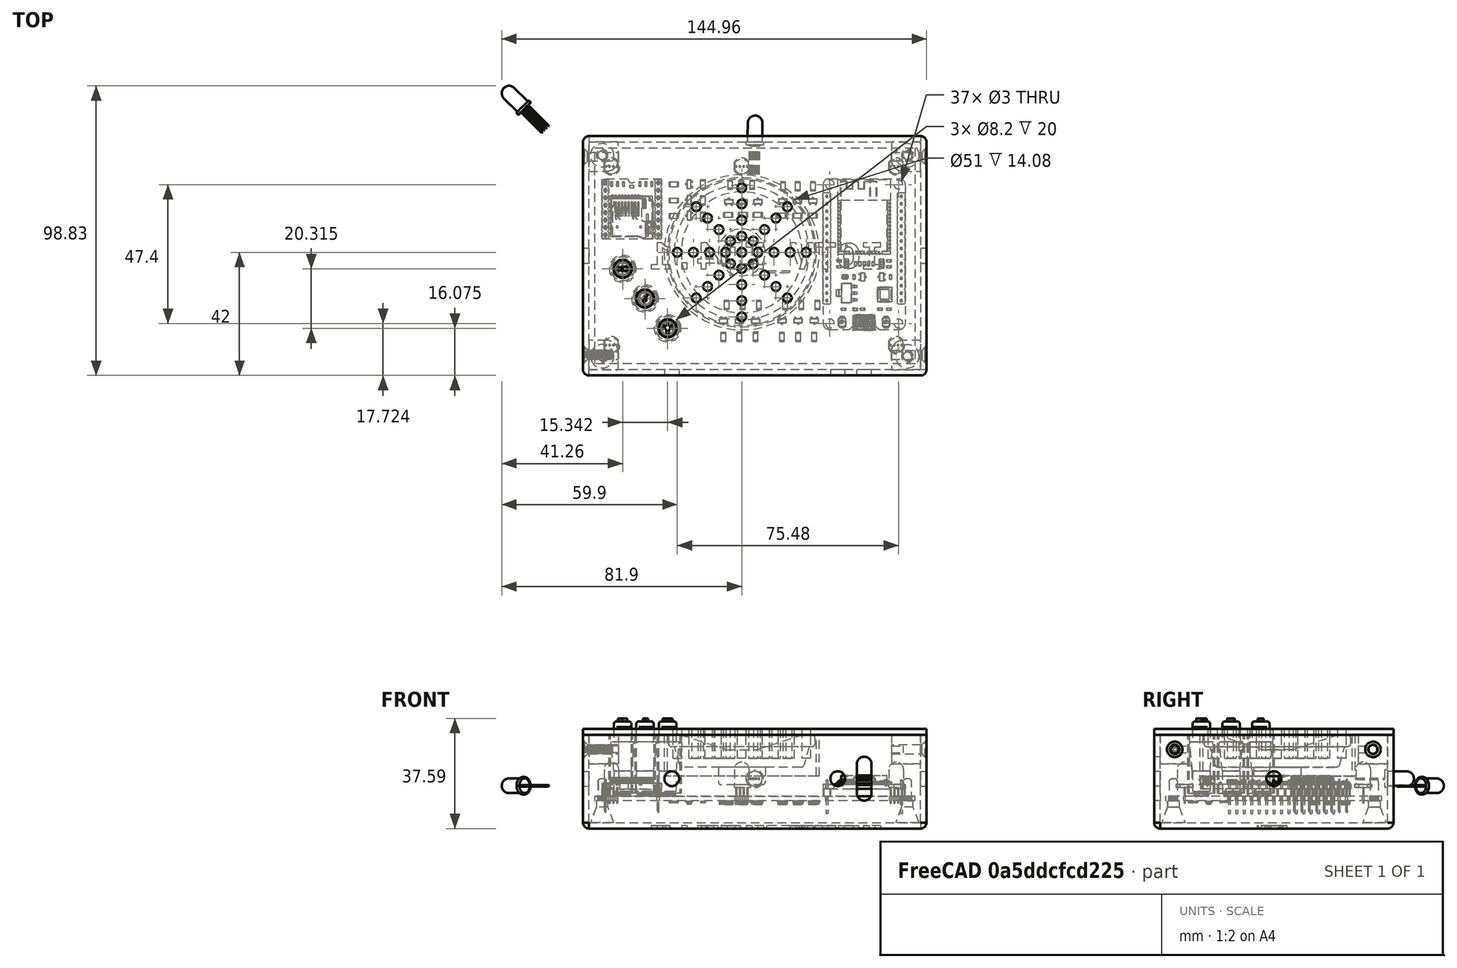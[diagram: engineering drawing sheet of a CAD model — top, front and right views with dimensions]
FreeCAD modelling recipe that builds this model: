
FCSTD DOCUMENT  (FreeCAD 0.20R)
Label: id4.1
License: All rights reserved
LicenseURL: http://en.wikipedia.org/wiki/All_rights_reserved
objects: PartDesign::Body×19, Part::Fillet×18, PartDesign::FeatureBase×17, Sketcher::SketchObject×15, Part::MultiFuse×13, Part::Cylinder×10, Part::FeaturePython×8, Part::Chamfer×8, Part::Extrusion×6, Part::Cut×6, PartDesign::Pocket×5, Part::Cone×4, PartDesign::ShapeBinder×4, Part::Box×4, App::Part×4, PartDesign::Fillet×2, PartDesign::Pad×2, Part::Compound×2, Part::Thickness×1, Part::Feature×1, +7 more types
note: 162 computed .brp shape members not serialized (recipe doc carries the construction recipe); baked Part::Feature solids carry a one-line shape summary decoded from their .brp

FEATURE [Sketcher::SketchObject] Sketch
  FullyConstrained = false
  MapMode = 5
  Placement = pos=(-170,95,8.58) rot=(0,0,1;0rad)
  sketch-geometry (4):
    g0: LineSegment StartX=114.84 StartY=-51.34 StartZ=0 EndX=228.06 EndY=-51.34 EndZ=0
    g1: LineSegment StartX=228.06 StartY=-51.34 StartZ=0 EndX=228.06 EndY=-129 EndZ=0
    g2: LineSegment StartX=228.06 StartY=-129 StartZ=0 EndX=114.84 EndY=-129 EndZ=0
    g3: LineSegment StartX=114.84 StartY=-129 StartZ=0 EndX=114.84 EndY=-51.34 EndZ=0
  constraints (8):
    c: Coincident(g0,g1)
    c: Coincident(g1,g2)
    c: Coincident(g2,g3)
    c: Coincident(g3,g0)
    c: Horizontal(g0)
    c: Horizontal(g2)
    c: Vertical(g1)
    c: Vertical(g3)
FEATURE [Part::Extrusion] Extrude
  Base = -> Sketch
  Dir = (0,0,1)
  DirMode = 2
  FaceMakerClass = Part::FaceMakerBullseye
  LengthFwd = 30
  LengthRev = 0
  Solid = true
  Symmetric = false
FEATURE [Part::Thickness] Thickness
  Faces = -> Extrude [Face6]
  Intersection = false
  Join = 0
  Mode = 0
  SelfIntersection = false
  Value = 2
FEATURE [Part::Feature] Feature001  label="Плата001"
  Placement = pos=(-170,95,16) rot=(0,0,1;0rad)
  shape: bbox 109.2 x 73.67 x 17.65 mm, 7789 faces, 158 solids (baked)
FEATURE [Part::FeaturePython] Screw001  label="M3x10-Винт001"  # Fasteners workbench fastener (typed FeaturePython)
  Placement = pos=(-57.16,-28.85,33.6) rot=(0,-1,0;1.5708rad)
  diameter = 4
  invert = false
  leftHanded = false
  length = 3
  lengthCustom = 10
  matchOuter = false
  offset = 0
  thread = true
  type = 47
FEATURE [Sketcher::SketchObject] Sketch004
  FullyConstrained = true
  MapMode = 5
  Placement = pos=(0,0,0) rot=(0.57735,0.57735,0.57735;2.0944rad)
  Support = -> [YZ_Plane]
FEATURE [Sketcher::SketchObject] Sketch001
  FullyConstrained = false
  MapMode = 5
  Placement = pos=(-170,95,17.58) rot=(0,0,1;0rad)
  Support = -> [Feature001]
  sketch-geometry (4):
    g0: Circle CenterX=119.361 CenterY=-55.8877 CenterZ=0 NormalX=0 NormalY=0 NormalZ=1 AngleXU=0 Radius=1.4
    g1: Circle CenterX=223.525 CenterY=-55.8927 CenterZ=0 NormalX=0 NormalY=0 NormalZ=1 AngleXU=0 Radius=1.4
    g2: Circle CenterX=119.376 CenterY=-124.461 CenterZ=0 NormalX=0 NormalY=0 NormalZ=1 AngleXU=0 Radius=1.4
    g3: Circle CenterX=223.508 CenterY=-124.479 CenterZ=0 NormalX=0 NormalY=0 NormalZ=1 AngleXU=0 Radius=1.4
  constraints (4):
    c: Diameter(g3) = 2.8
    c: Diameter(g2) = 2.8
    c: Diameter(g0) = 2.8
    c: Diameter(g1) = 2.8
FEATURE [Part::Extrusion] Extrude001
  Base = -> Sketch001
  Dir = (0,0,1)
  DirMode = 2
  FaceMakerClass = Part::FaceMakerBullseye
  LengthFwd = 15
  LengthRev = 0
  Placement = pos=(0,0,-9) rot=(0,0,1;0rad)
  Solid = true
  Symmetric = false
FEATURE [Part::Fillet] Fillet
  Base = -> Extrude001
  Edges = 1 edges r=1: [Edge6]
FEATURE [Part::Fillet] Fillet001
  Base = -> Fillet
  Edges = 1 edges r=1: [Edge13]
FEATURE [Part::Cone] Cone  label="Конус"
  Angle = 360
  AttacherType = Attacher::AttachEngine3D
  Height = 8
  Placement = pos=(-50.62,-29.46,8.58) rot=(0,0,1;0rad)
  Radius1 = 4
  Radius2 = 1
FEATURE [Part::Cylinder] Cylinder  label="Цилиндр"
  Angle = 360
  AttacherType = Attacher::AttachEngine3D
  FirstAngle = 0
  Height = 2.5
  Placement = pos=(-50.624,-29.4614,13.58) rot=(0,0,1;0rad)
  Radius = 2
  SecondAngle = 0
FEATURE [Part::Fillet] Fillet002
  Base = -> Fillet001
  Edges = 1 edges r=1: [Edge15]
FEATURE [Part::MultiFuse] Fusion
  Placement = pos=(-0.019282,68.5723,-1.8e-15) rot=(0,0,1;0rad)
  Shapes = -> [Cone,Cylinder]
FEATURE [Part::FeaturePython] Clone  label="Fusion001"  # Draft clone (typed FeaturePython)
  AttacherType = Attacher::AttachEngine3D
  Fuse = false
  Objects = -> [Fusion]
  Placement = pos=(104.145,68.5673,-1.8e-15) rot=(0,0,1;0rad)
  Scale = (1,1,1)
FEATURE [Part::FeaturePython] Clone001  label="Fusion002"  # Draft clone (typed FeaturePython)
  AttacherType = Attacher::AttachEngine3D
  Fuse = false
  Objects = -> [Clone]
  Placement = pos=(104.128,-0.018798,-1.8e-15) rot=(0,0,1;0rad)
  Scale = (1,1,1)
FEATURE [Part::FeaturePython] Clone002  label="Fusion003"  # Draft clone (typed FeaturePython)
  AttacherType = Attacher::AttachEngine3D
  Fuse = false
  Objects = -> [Clone001]
  Scale = (1,1,1)
FEATURE [Part::Fillet] Fillet003
  Base = -> Fillet002
  Edges = 1 edges r=1: [Edge17]
FEATURE [Part::Fillet] Fillet004
  Base = -> Fusion
  Edges = 1 edges r=0.5: [Edge4]
FEATURE [Part::Fillet] Fillet005
  Base = -> Clone002
  Edges = 1 edges r=0.5: [Edge4]
FEATURE [Part::Fillet] Fillet006
  Base = -> Clone001
  Edges = 1 edges r=0.5: [Edge4]
FEATURE [Part::Fillet] Fillet007
  Base = -> Clone
  Edges = 1 edges r=0.5: [Edge4]
FEATURE [Part::MultiFuse] Fusion001  label="Fusion004"
  Shapes = -> [Fillet007,Fillet003,Fillet004,Fillet005,Fillet006]
FEATURE [Part::MultiFuse] Fusion002  label="зависимость"
  Placement = pos=(6.25,0.25,-0.733338) rot=(0,0,1;0rad)
  Shapes = -> [Fusion001,Thickness]
FEATURE [PartDesign::FeatureBase] BaseFeature
  BaseFeature = -> Fusion002
FEATURE [PartDesign::Body] Body  label="корпус"
  BaseFeature = -> Fusion002
  Group = -> [BaseFeature,Sketch004]
  Origin = -> Origin
  Tip = -> BaseFeature
FEATURE [Sketcher::SketchObject] Sketch002
  ExternalGeometry = -> [BaseFeature]
  FullyConstrained = false
  MapMode = 5
  Support = -> [XY_Plane]
  sketch-geometry (8):
    g0: LineSegment StartX=58.06 StartY=45.66 StartZ=0 EndX=-55.16 EndY=45.66 EndZ=0
    g1: LineSegment StartX=-57.16 StartY=43.66 StartZ=0 EndX=-57.16 EndY=-34 EndZ=0
    g2: LineSegment StartX=-55.16 StartY=-36 StartZ=0 EndX=58.06 EndY=-36 EndZ=0
    g3: ArcOfCircle CenterX=-55.16 CenterY=43.66 CenterZ=0 NormalX=0 NormalY=0 NormalZ=1 AngleXU=0 Radius=2 StartAngle=1.5708 EndAngle=3.14159
    g4: ArcOfCircle CenterX=-55.16 CenterY=-34 CenterZ=0 NormalX=0 NormalY=0 NormalZ=1 AngleXU=0 Radius=2 StartAngle=3.14159 EndAngle=4.71239
    g5: LineSegment StartX=60.06 StartY=-34 StartZ=0 EndX=60.06 EndY=43.66 EndZ=0
    g6: ArcOfCircle CenterX=58.06 CenterY=43.66 CenterZ=0 NormalX=0 NormalY=0 NormalZ=1 AngleXU=0 Radius=2 StartAngle=-2.22e-14 EndAngle=1.5708
    g7: ArcOfCircle CenterX=58.06 CenterY=-34 CenterZ=0 NormalX=0 NormalY=0 NormalZ=1 AngleXU=0 Radius=2 StartAngle=4.71239 EndAngle=6.28319
  constraints (18):
    c: Coincident(g0,g-10)
    c: Coincident(g0,g-4)
    c: Coincident(g1,g-5)
    c: Coincident(g1,g-6)
    c: Coincident(g2,g-7)
    c: Coincident(g2,g-8)
    c: Coincident(g3,g1)
    c: Coincident(g3,g0)
    c: Coincident(g4,g2)
    c: Coincident(g4,g1)
    c: Tangent(g4,g-6)
    c: Coincident(g5,g-9)
    c: Coincident(g5,g-10)
    c: Coincident(g6,g5)
    c: Coincident(g6,g0)
    c: Tangent(g6,g-10)
    c: Coincident(g7,g2)
    c: Coincident(g7,g5)
FEATURE [Part::Extrusion] Extrude002  label="крышка"
  Base = -> Sketch002
  Dir = (0,0,1)
  DirMode = 2
  FaceMakerClass = Part::FaceMakerBullseye
  LengthFwd = 2
  LengthRev = 0
  Placement = pos=(0,0,39) rot=(0,0,1;0rad)
  Solid = true
  Symmetric = false
FEATURE [PartDesign::FeatureBase] BaseFeature001
  BaseFeature = -> Extrude002
  Placement = pos=(0,7.1e-15,-1.42) rot=(0,0,1;0rad)
FEATURE [PartDesign::Body] Body001  label="Крышка"
  BaseFeature = -> Extrude002
  Group = -> [BaseFeature001]
  Origin = -> Origin001
  Placement = pos=(0,0,40) rot=(0,0,1;0rad)
  Tip = -> BaseFeature001
FEATURE [Sketcher::SketchObject] Sketch003
  ExternalGeometry = -> [BaseFeature]
  FullyConstrained = true
  MapMode = 5
  Placement = pos=(0,0,38.58) rot=(0,0,1;0rad)
  Support = -> [BaseFeature]
  sketch-geometry (4):
    g0: LineSegment StartX=-55.16 StartY=-34 StartZ=0 EndX=-45.16 EndY=-34 EndZ=0
    g1: LineSegment StartX=-45.16 StartY=-34 StartZ=0 EndX=-45.16 EndY=-24 EndZ=0
    g2: LineSegment StartX=-45.16 StartY=-24 StartZ=0 EndX=-55.16 EndY=-24 EndZ=0
    g3: LineSegment StartX=-55.16 StartY=-24 StartZ=0 EndX=-55.16 EndY=-34 EndZ=0
  constraints (11):
    c: Coincident(g0,g1)
    c: Coincident(g1,g2)
    c: Coincident(g2,g3)
    c: Coincident(g3,g0)
    c: Horizontal(g0)
    c: Horizontal(g2)
    c: Vertical(g1)
    c: Vertical(g3)
    c: Coincident(g0,g-4)
    c: Distance(g2) = 10
    c: Distance(g3) = 10
FEATURE [Part::Extrusion] Extrude003
  Base = -> Sketch003
  Dir = (0,0,1)
  DirMode = 2
  FaceMakerClass = Part::FaceMakerBullseye
  LengthFwd = 10
  LengthRev = 0
  Reversed = true
  Solid = true
  Symmetric = false
FEATURE [PartDesign::ShapeBinder] ShapeBinder
  Placement = pos=(-57.16,-28.85,33.6) rot=(0,-1,0;1.5708rad)
  Support = -> [Screw001]
  TraceSupport = false
FEATURE [PartDesign::ShapeBinder] ShapeBinder001
  Placement = pos=(-57.16,-28.85,33.6) rot=(0,-1,0;1.5708rad)
  Support = -> [Screw001]
  TraceSupport = false
FEATURE [PartDesign::ShapeBinder] ShapeBinder002
  Placement = pos=(-57.16,-28.85,33.6) rot=(0,-1,0;1.5708rad)
  Support = -> [Screw001]
  TraceSupport = false
FEATURE [PartDesign::ShapeBinder] ShapeBinder003
  Placement = pos=(-57.16,-28.85,33.6) rot=(0,-1,0;1.5708rad)
  Support = -> [Screw001]
  TraceSupport = false
FEATURE [Part::Loft] Loft
  Closed = false
  MaxDegree = 5
  Placement = pos=(0,-0.15,-0.02) rot=(0,0,1;0rad)
  Ruled = true
  Sections = -> [ShapeBinder,ShapeBinder003,ShapeBinder001,ShapeBinder002]
  Solid = true
FEATURE [PartDesign::FeatureBase] Clone003
  BaseFeature = -> Loft
  Placement = pos=(26.1,-88.15,-67.18) rot=(0,0,1;0rad)
FEATURE [PartDesign::Body] Body003
  BaseFeature = -> Loft
  Group = -> [Clone003]
  Origin = -> Origin003
  Placement = pos=(29,88,0) rot=(0,1,0;3.14159rad)
  Tip = -> Clone003
FEATURE [PartDesign::FeatureBase] Clone004
  BaseFeature = -> Loft
  Placement = pos=(8,15.51,-0.02) rot=(0,0,1;0rad)
FEATURE [PartDesign::Body] Body004
  BaseFeature = -> Loft
  Group = -> [Clone004]
  Origin = -> Origin004
  Placement = pos=(-8,52,0) rot=(0,0,1;0rad)
  Tip = -> Clone004
FEATURE [PartDesign::FeatureBase] Clone005
  BaseFeature = -> Loft
  Placement = pos=(67.1,-33.49,-67.18) rot=(0,0,1;0rad)
FEATURE [PartDesign::Body] Body005
  BaseFeature = -> Loft
  Group = -> [Clone005]
  Origin = -> Origin005
  Placement = pos=(70,101,0) rot=(0,1,0;3.14159rad)
  Tip = -> Clone005
FEATURE [PartDesign::FeatureBase] Clone006
  BaseFeature = -> Extrude003
  Placement = pos=(58.22,-6,0) rot=(0,0,1;0rad)
FEATURE [PartDesign::Body] Body006
  BaseFeature = -> Extrude003
  Group = -> [Clone006]
  Origin = -> Origin006
  Placement = pos=(45,6,0) rot=(0,0,1;0rad)
  Tip = -> Clone006
FEATURE [PartDesign::FeatureBase] Clone007
  BaseFeature = -> Extrude003
  Placement = pos=(-10,27.66,0) rot=(0,0,1;0rad)
FEATURE [PartDesign::Body] Body007
  BaseFeature = -> Extrude003
  Group = -> [Clone007]
  Origin = -> Origin007
  Placement = pos=(10,40,0) rot=(0,0,1;0rad)
  Tip = -> Clone007
FEATURE [PartDesign::FeatureBase] Clone008
  BaseFeature = -> Extrude003
  Placement = pos=(89.22,45.66,0) rot=(0,0,1;0rad)
FEATURE [PartDesign::Body] Body008
  BaseFeature = -> Extrude003
  Group = -> [Clone008]
  Origin = -> Origin008
  Placement = pos=(14,22,0) rot=(0,0,1;0rad)
  Tip = -> Clone008
FEATURE [Part::Cylinder] Cylinder001  label="Цилиндр001"
  Angle = 360
  AttacherType = Attacher::AttachEngine3D
  FirstAngle = 0
  Height = 141
  Placement = pos=(69.84,-29,33.58) rot=(0,-1,0;1.5708rad)
  Radius = 1.5
  SecondAngle = 0
FEATURE [Part::FeaturePython] Clone009  label="Цилиндр002"  # Draft clone (typed FeaturePython)
  AttacherType = Attacher::AttachEngine3D
  Fuse = false
  Objects = -> [Cylinder001]
  Placement = pos=(73.06,38.66,33.58) rot=(0,-1,0;1.5708rad)
  Scale = (1,1,1)
FEATURE [Part::MultiFuse] Fusion003  label="Fusion006"
  Shapes = -> [Body008,Body007,Body006,Extrude003]
FEATURE [Part::MultiFuse] Fusion004  label="Fusion007"
  Shapes = -> [Loft,Body003,Body004,Body005]
FEATURE [Part::Cut] Cut
  Base = -> Body
  Tool = -> Fusion004
FEATURE [PartDesign::FeatureBase] Clone010
  BaseFeature = -> Clone009
  Placement = pos=(73.06,38.66,33.58) rot=(0,-1,0;1.5708rad)
FEATURE [PartDesign::Body] Body009
  BaseFeature = -> Clone009
  Group = -> [Clone010]
  Origin = -> Origin009
  Tip = -> Clone010
FEATURE [PartDesign::FeatureBase] Clone011
  BaseFeature = -> Cylinder001
  Placement = pos=(69.84,-29,33.58) rot=(0,-1,0;1.5708rad)
FEATURE [PartDesign::Body] Body010
  BaseFeature = -> Cylinder001
  Group = -> [Clone011]
  Origin = -> Origin010
  Tip = -> Clone011
FEATURE [Part::Cut] Cut001
  Base = -> Cut
  Tool = -> Clone009
FEATURE [Part::Cut] Cut002  label="зависимость корпус001"
  Base = -> Cut001
  Tool = -> Cylinder001
FEATURE [Part::MultiFuse] Fusion005  label="Fusion008"
  Shapes = -> [Body009,Body010]
FEATURE [Part::Cut] Cut003
  Base = -> Fusion003
  Tool = -> Fusion005
FEATURE [Part::MultiFuse] Fusion006  label="зависимость001"
  Shapes = -> [Cut003,Body001]
FEATURE [PartDesign::FeatureBase] Clone012
  BaseFeature = -> Fusion006
FEATURE [PartDesign::Body] Body011  label="крышка002"
  BaseFeature = -> Fusion006
  Group = -> [Clone012]
  Origin = -> Origin013
  Tip = -> Clone012
FEATURE [Part::Box] Box004  label="Куб004"
  AttacherType = Attacher::AttachEngine3D
  Height = 10
  Length = 0.5
  Placement = pos=(-2,-0.25,-10) rot=(0,0,1;0rad)
  Width = 0.5
FEATURE [Part::Box] Box005  label="Куб005"
  AttacherType = Attacher::AttachEngine3D
  Height = 10
  Length = 0.5
  Placement = pos=(-2,-0.25,-10) rot=(0,0,1;0rad)
  Width = 0.5
FEATURE [Part::Box] Box006  label="Куб006"
  AttacherType = Attacher::AttachEngine3D
  Height = 10
  Length = 0.5
  Placement = pos=(-2,-0.25,-10) rot=(0,0,1;0rad)
  Width = 0.5
FEATURE [Part::Box] Box007  label="Куб007"
  AttacherType = Attacher::AttachEngine3D
  Height = 10
  Length = 0.5
  Placement = pos=(-2,-0.25,-10) rot=(0,0,1;0rad)
  Width = 0.5
FEATURE [Part::Chamfer] Chamfer008
  Base = -> Box004
  Edges = 1 edges r=0.2: [Edge9]
FEATURE [Part::Chamfer] Chamfer009
  Base = -> Chamfer008
  Edges = 1 edges r=0.2: [Edge14]
FEATURE [Part::Chamfer] Chamfer010
  Base = -> Box005
  Edges = 1 edges r=0.2: [Edge9]
FEATURE [Part::Chamfer] Chamfer011
  Base = -> Chamfer010
  Edges = 1 edges r=0.2: [Edge14]
  Placement = pos=(1,0,0) rot=(0,0,1;0rad)
FEATURE [Part::Chamfer] Chamfer012
  Base = -> Box006
  Edges = 1 edges r=0.2: [Edge9]
FEATURE [Part::Chamfer] Chamfer013
  Base = -> Chamfer012
  Edges = 1 edges r=0.2: [Edge14]
  Placement = pos=(2,0,0) rot=(0,0,1;0rad)
FEATURE [Part::Chamfer] Chamfer014
  Base = -> Box007
  Edges = 1 edges r=0.2: [Edge9]
FEATURE [Part::Chamfer] Chamfer015
  Base = -> Chamfer014
  Edges = 1 edges r=0.2: [Edge14]
  Placement = pos=(3,0,0) rot=(0,0,1;0rad)
FEATURE [Part::Cylinder] Cylinder021  label="Цилиндр021"
  Angle = 360
  AttacherType = Attacher::AttachEngine3D
  FirstAngle = 0
  Height = 10
  Radius = 2.5
  SecondAngle = 0
FEATURE [Part::Cylinder] Cylinder022  label="Цилиндр022"
  Angle = 360
  AttacherType = Attacher::AttachEngine3D
  FirstAngle = 0
  Height = 1
  Radius = 3
  SecondAngle = 0
FEATURE [Part::Fillet] Fillet014
  Base = -> Cylinder022
  Edges = 2 edges r=0.2: [Edge2,Edge3]
FEATURE [Part::MultiFuse] Fusion014
  Placement = pos=(0.25,0,0) rot=(0,0,1;0rad)
  Shapes = -> [Chamfer015,Chamfer009,Chamfer011,Chamfer013]
FEATURE [Sketcher::SketchObject] Sketch013
  FullyConstrained = true
  Placement = pos=(0,0,0) rot=(1,0,0;1.5708rad)
  sketch-geometry (10):
    g0: LineSegment StartX=0 StartY=0 StartZ=0 EndX=-25 EndY=0 EndZ=0
    g1: LineSegment StartX=-25 StartY=0 StartZ=0 EndX=-25 EndY=4 EndZ=0
    g2: LineSegment StartX=-25 StartY=4 StartZ=0 EndX=-23 EndY=4 EndZ=0
    g3: LineSegment StartX=-23 StartY=4 StartZ=0 EndX=-21 EndY=11 EndZ=0
    g4: LineSegment StartX=-21 StartY=11 StartZ=0 EndX=0 EndY=11 EndZ=0
    g5: LineSegment StartX=-21 StartY=11 StartZ=0 EndX=-21 EndY=0 EndZ=0
    g6: LineSegment StartX=-21 StartY=11 StartZ=0 EndX=-8 EndY=11 EndZ=0
    g7: LineSegment StartX=-8 StartY=11 StartZ=0 EndX=-8 EndY=17 EndZ=0
    g8: LineSegment StartX=-8 StartY=17 StartZ=0 EndX=0 EndY=17 EndZ=0
    g9: LineSegment StartX=0 StartY=17 StartZ=0 EndX=0 EndY=0 EndZ=0
  constraints (29):
    c: Coincident(g0,g-1)
    c: PointOnObject(g0,g-1)
    c: Coincident(g1,g0)
    c: Vertical(g1)
    c: Distance(g0) = 25
    c: Distance(g1) = 4
    c: Coincident(g2,g1)
    c: Horizontal(g2)
    c: Distance(g2) = 2
    c: Coincident(g3,g2)
    c: Coincident(g4,g3)
    c: PointOnObject(g4,g-2)
    c: Horizontal(g4)
    c: Distance(g4) = 21
    c: Coincident(g5,g3)
    c: PointOnObject(g5,g0)
    c: Vertical(g5)
    c: Distance(g5) = 11
    c: Coincident(g6,g3)
    c: PointOnObject(g6,g4)
    c: Distance(g6,g4) = 8
    c: Coincident(g7,g6)
    c: Vertical(g7)
    c: Distance(g7) = 6
    c: Coincident(g8,g7)
    c: Horizontal(g8)
    c: PointOnObject(g8,g-2)
    c: Coincident(g9,g8)
    c: Coincident(g9,g0)
FEATURE [Part::Revolution] Revolve
  Angle = 360
  Axis = (0,0,1)
  Base = (0,0,0)
  FaceMakerClass = Part::FaceMakerBullseye
  Solid = true
  Source = -> Sketch013
  Symmetric = false
FEATURE [Part::Fillet] Fillet017
  Base = -> Revolve
  Edges = 2 edges r=1: [Edge5,Edge8]
FEATURE [Part::Fillet] Fillet018
  Base = -> Fillet017
  Edges = 1 edges r=1: [Edge6]
FEATURE [PartDesign::FeatureBase] BaseFeature002
  BaseFeature = -> Fillet018
FEATURE [Sketcher::SketchObject] Sketch014
  FullyConstrained = false
  MapMode = 5
  Placement = pos=(0,0,0) rot=(1,0,0;3.14159rad)
  Support = -> [BaseFeature002]
  sketch-geometry (1):
    g0: Circle CenterX=0 CenterY=0 CenterZ=0 NormalX=0 NormalY=0 NormalZ=1 AngleXU=0 Radius=20.6628
  constraints (1):
    c: Coincident(g0,g-1)
FEATURE [PartDesign::Pocket] Pocket
  BaseFeature = -> BaseFeature002
  Direction = (0,0,1)
  Length = 5
  Length2 = 5
  Profile = -> Sketch014
  ReferenceAxis = -> Sketch014 [N_Axis]
  TaperAngle = -72
  Type = 0
FEATURE [PartDesign::Fillet] Fillet019
  Base = -> Pocket [Edge8]
  BaseFeature = -> Pocket
  Radius = 1
  SupportTransform = false
  UseAllEdges = false
FEATURE [PartDesign::Body] Body014  label="динамик"
  BaseFeature = -> Fillet018
  Group = -> [BaseFeature002,Sketch014,Pocket,Fillet019]
  Origin = -> Origin016
  Placement = pos=(-3,6,38.5) rot=(0,1,0;3.14159rad)
  Tip = -> Fillet019
FEATURE [Sketcher::SketchObject] Sketch015
  FullyConstrained = true
  MapMode = 5
  Support = -> [XY_Plane017]
  sketch-geometry (1):
    g0: Circle CenterX=0 CenterY=0 CenterZ=0 NormalX=0 NormalY=0 NormalZ=1 AngleXU=0 Radius=25.5
  constraints (2):
    c: Coincident(g0,g-1)
    c: Diameter(g0) = 51
FEATURE [PartDesign::Pad] Pad
  Direction = (0,0,1)
  Length = 15
  Length2 = 10
  Profile = -> Sketch015
  ReferenceAxis = -> Sketch015 [N_Axis]
  Type = 0
FEATURE [PartDesign::Thickness] Thickness001
  Base = -> Pad [Face2]
  BaseFeature = -> Pad
  Intersection = false
  Join = 0
  Mode = 0
  SupportTransform = false
  Value = 1
FEATURE [PartDesign::Body] Body015  label="капсулю динамика"
  Group = -> [Sketch015,Pad,Thickness001]
  Origin = -> Origin017
  Placement = pos=(-3,6,24.5) rot=(0,0,1;0rad)
  Tip = -> Thickness001
FEATURE [PartDesign::AdditiveCylinder] Cylinder023
  Angle = 360
  AttacherType = Attacher::AttachEngine3D
  FirstAngle = 0
  Height = 10
  Placement = pos=(-3,6,30.5) rot=(0,0,1;0rad)
  Radius = 1.5
  SecondAngle = 0
FEATURE [Part::FeaturePython] Array  # Draft array (typed FeaturePython)
  AlwaysSyncPlacement = false
  Angle = 360
  ArrayType = 0
  Axis = (0,0,1)
  Base = -> Cylinder023
  Center = (0,0,0)
  Count = 5
  ExpandArray = false
  Fuse = false
  IntervalAxis = (0,0,0)
  IntervalX = (5.5,0,0)
  IntervalY = (0,100,0)
  IntervalZ = (0,0,100)
  NumberCircles = 3
  NumberPolar = 5
  NumberX = 5
  NumberY = 1
  NumberZ = 1
  PlacementList = 5 placements: arithmetic series from (-3,6,30.5) step (5.5,0,0) to (19,6,30.5)
  RadialDistance = 50
  ScaleList = (5) [(1,1,1),(1,1,1),(1,1,1),(1,1,1),(1,1,1)]
  Symmetry = 1
  TangentialDistance = 25
FEATURE [Part::FeaturePython] Array001  # Draft array (typed FeaturePython)
  AlwaysSyncPlacement = false
  Angle = 360
  ArrayType = 1
  Axis = (0,0,1)
  Base = -> Array
  Center = (-3,6,39.5)
  Count = 8
  ExpandArray = false
  Fuse = false
  IntervalAxis = (0,0,0)
  IntervalX = (50,0,0)
  IntervalY = (0,50,0)
  IntervalZ = (0,0,50)
  NumberCircles = 2
  NumberPolar = 8
  NumberX = 2
  NumberY = 2
  NumberZ = 1
  Placement = pos=(0,0,7) rot=(0,0,1;0rad)
  PlacementList = 8 placements: [(0,0,0),(3.36396,3.87868,0),(3,9,0),(-0.87868,12.364,0),(-6,12,0),(-9.36396,8.12132,0),(-9,3,0),(-5.12132,-0.363961,0)]
  RadialDistance = 20
  ScaleList = (8) [(1,1,1),(1,1,1),(1,1,1),(1,1,1),(1,1,1),(1,1,1),(1,1,1),(1,1,1)]
  Symmetry = 1
  TangentialDistance = 15
FEATURE [Part::FeaturePython] Clone016  label="Array002"  # Draft clone (typed FeaturePython)
  AttacherType = Attacher::AttachEngine3D
  Fuse = false
  Objects = -> [Array001]
  Scale = (1,1,1)
FEATURE [Part::MultiFuse] Fusion015
  Shapes = -> [Body011,Body015]
FEATURE [Part::Cut] Cut004
  Base = -> Fusion015
  Tool = -> Array001
FEATURE [PartDesign::FeatureBase] Clone017
  BaseFeature = -> Cut004
FEATURE [PartDesign::FeatureBase] Clone018
  BaseFeature = -> Cut002
FEATURE [Part::Fillet] Fillet013
  Base = -> Cylinder021
  Edges = 1 edges r=2.5: [Edge3]
FEATURE [Part::Compound] Compound006
  Links = -> [Fusion014,Fillet014,Fillet013]
  Placement = pos=(-77.1,55.03,21.17) rot=(-0.281085,0.678598,0.678598;3.68962rad)
FEATURE [PartDesign::Boolean] Boolean001
  Group = -> [Chamfer008,Chamfer010,Fillet013,Chamfer011,Chamfer012,Compound006,Cylinder022,Chamfer013,Chamfer014,Chamfer015,Fusion014,Fillet014,Box004,Cylinder021,Box005,Box006,Box007,Chamfer009]
  Placement = pos=(12.1122,-20.0773,-7.88146) rot=(0,0,1;0rad)
  Type = 0
FEATURE [PartDesign::Body] Body013
  Group = -> [Boolean001]
  Origin = -> Origin015
  Placement = pos=(21.434,-28.3683,10.2915) rot=(0,0,-1;0.802851rad)
  Tip = -> Boolean001
FEATURE [App::Part] Part002  label="не печатать"
  Group = -> [Fillet018,Revolve,Fillet017,Sketch013,Body014,Body013,Fusion002,Cylinder,Sketch,Thickness,Fillet002,Extrude001,Clone001,Sketch001,Fusion001,Extrude,Clone,Clone002,Fillet,Fillet005,Fillet004,Fillet001,Fillet007,Fillet006,Cone,Fusion,Fillet003,Feature001]
  Origin = -> Origin019
FEATURE [Sketcher::SketchObject] Sketch016
  ExternalGeometry = -> [Clone018]
  FullyConstrained = true
  MapMode = 5
  Placement = pos=(0,-36,0) rot=(1,0,0;1.5708rad)
  Support = -> [Cut002]
  sketch-geometry (12):
    g0: LineSegment StartX=-55.16 StartY=38.58 StartZ=0 EndX=58.06 EndY=8.58 EndZ=0
    g1: LineSegment StartX=-55.16 StartY=8.58 StartZ=0 EndX=58.06 EndY=38.58 EndZ=0
    g2: GeomPoint X=1.45 Y=23.58 Z=0
    g3: LineSegment StartX=1.45 StartY=8.58 StartZ=0 EndX=1.45 EndY=38.58 EndZ=0
    g4: LineSegment StartX=-55.16 StartY=38.58 StartZ=0 EndX=1.45 EndY=8.58 EndZ=0
    g5: LineSegment StartX=-55.16 StartY=8.58 StartZ=0 EndX=1.45 EndY=38.58 EndZ=0
    g6: LineSegment StartX=1.45 StartY=8.58 StartZ=0 EndX=58.06 EndY=38.58 EndZ=0
    g7: LineSegment StartX=58.06 StartY=8.58 StartZ=0 EndX=1.45 EndY=38.58 EndZ=0
    g8: GeomPoint X=29.755 Y=23.58 Z=0
    g9: Circle CenterX=29.755 CenterY=23.58 CenterZ=0 NormalX=0 NormalY=0 NormalZ=1 AngleXU=0 Radius=2.525
    g10: GeomPoint X=-26.855 Y=23.58 Z=0
    g11: Circle CenterX=-26.855 CenterY=23.58 CenterZ=0 NormalX=0 NormalY=0 NormalZ=1 AngleXU=0 Radius=2.525
  constraints (26):
    c: Coincident(g0,g-5)
    c: Coincident(g0,g-6)
    c: Coincident(g1,g-6)
    c: Coincident(g1,g-5)
    c: PointOnObject(g2,g1)
    c: PointOnObject(g2,g0)
    c: PointOnObject(g3,g-6)
    c: PointOnObject(g3,g-5)
    c: Vertical(g3)
    c: PointOnObject(g2,g3)
    c: Coincident(g4,g0)
    c: Coincident(g4,g3)
    c: Coincident(g5,g1)
    c: Coincident(g5,g3)
    c: Coincident(g6,g3)
    c: Coincident(g6,g1)
    c: Coincident(g7,g0)
    c: Coincident(g7,g3)
    c: PointOnObject(g8,g7)
    c: PointOnObject(g8,g6)
    c: Coincident(g9,g8)
    c: Diameter(g9) = 5.05
    c: PointOnObject(g10,g5)
    c: PointOnObject(g10,g4)
    c: Coincident(g11,g10)
    c: Diameter(g11) = 5.05
FEATURE [PartDesign::Pocket] Pocket001
  BaseFeature = -> Clone018
  Direction = (0,1,-2e-16)
  Length = 9
  Length2 = 5
  Profile = -> Sketch016
  ReferenceAxis = -> Sketch016 [N_Axis]
  Type = 0
FEATURE [Sketcher::SketchObject] Sketch017
  ExternalGeometry = -> [Pocket001]
  FullyConstrained = true
  MapMode = 5
  Placement = pos=(0,43.66,0) rot=(1,0,0;1.5708rad)
  Support = -> [Pocket001]
  sketch-geometry (4):
    g0: LineSegment StartX=-55.16 StartY=38.58 StartZ=0 EndX=58.06 EndY=8.58 EndZ=0
    g1: LineSegment StartX=58.06 StartY=38.58 StartZ=0 EndX=-55.16 EndY=8.58 EndZ=0
    g2: GeomPoint X=1.45 Y=23.58 Z=0
    g3: Circle CenterX=1.45 CenterY=23.58 CenterZ=0 NormalX=0 NormalY=0 NormalZ=1 AngleXU=0 Radius=2.525
  constraints (8):
    c: Coincident(g0,g-5)
    c: Coincident(g0,g-6)
    c: Coincident(g1,g-5)
    c: Coincident(g1,g-6)
    c: PointOnObject(g2,g0)
    c: PointOnObject(g2,g1)
    c: Coincident(g3,g2)
    c: Diameter(g3) = 5.05
FEATURE [PartDesign::Pocket] Pocket002
  BaseFeature = -> Pocket001
  Direction = (0,1,-2e-16)
  Length = 5
  Length2 = 5
  Profile = -> Sketch017
  ReferenceAxis = -> Sketch017 [N_Axis]
  Type = 0
FEATURE [Sketcher::SketchObject] Sketch018
  ExternalGeometry = -> [Pocket002]
  FullyConstrained = true
  MapMode = 5
  Placement = pos=(60.06,0,0) rot=(0.57735,0.57735,0.57735;2.0944rad)
  Support = -> [Pocket002]
  sketch-geometry (4):
    g0: LineSegment StartX=-34 StartY=38.58 StartZ=0 EndX=43.66 EndY=8.58 EndZ=0
    g1: LineSegment StartX=-34 StartY=8.58 StartZ=0 EndX=43.66 EndY=38.58 EndZ=0
    g2: GeomPoint X=4.83 Y=23.58 Z=0
    g3: Circle CenterX=4.83 CenterY=23.58 CenterZ=0 NormalX=0 NormalY=0 NormalZ=1 AngleXU=0 Radius=2.525
  constraints (8):
    c: Coincident(g0,g-3)
    c: Coincident(g0,g-4)
    c: Coincident(g1,g-3)
    c: Coincident(g1,g-4)
    c: PointOnObject(g2,g0)
    c: PointOnObject(g2,g1)
    c: Coincident(g3,g2)
    c: Diameter(g3) = 5.05
FEATURE [PartDesign::Pocket] Pocket003
  BaseFeature = -> Pocket002
  Direction = (-1,0,0)
  Length = 150
  Length2 = 5
  Profile = -> Sketch018
  ReferenceAxis = -> Sketch018 [N_Axis]
  Type = 0
FEATURE [Sketcher::SketchObject] Sketch019
  ExternalGeometry = -> [Pocket003]
  FullyConstrained = false
  MapMode = 5
  Placement = pos=(0,-36,0) rot=(1,0,0;1.5708rad)
  Support = -> [Pocket003]
  sketch-geometry (6):
    g0: ArcOfCircle CenterX=38.8008 CenterY=28.58 CenterZ=0 NormalX=0 NormalY=0 NormalZ=1 AngleXU=0 Radius=2.5 StartAngle=-1.59e-13 EndAngle=3.14159
    g1: ArcOfCircle CenterX=38.8008 CenterY=18.58 CenterZ=0 NormalX=0 NormalY=0 NormalZ=1 AngleXU=0 Radius=2.5 StartAngle=3.14159 EndAngle=6.28319
    g2: LineSegment StartX=36.3008 StartY=28.58 StartZ=0 EndX=36.3008 EndY=18.58 EndZ=0
    g3: LineSegment StartX=41.3008 StartY=18.58 StartZ=0 EndX=41.3008 EndY=28.58 EndZ=0
    g4: LineSegment StartX=38.8008 StartY=28.58 StartZ=0 EndX=38.8008 EndY=38.58 EndZ=0
    g5: LineSegment StartX=38.8008 StartY=18.58 StartZ=0 EndX=38.8008 EndY=8.58 EndZ=0
  constraints (15):
    c: Tangent(g0,g2) = -1.5708
    c: Tangent(g2,g1) = -1.5708
    c: Tangent(g1,g3) = -1.5708
    c: Tangent(g3,g0) = -1.5708
    c: Equal(g0,g1)
    c: Vertical(g2)
    c: DistanceY(g1,g0) = 10
    c: DistanceX(g1,g1) = 5
    c: Coincident(g4,g0)
    c: PointOnObject(g4,g-3)
    c: Vertical(g4)
    c: Coincident(g5,g1)
    c: PointOnObject(g5,g-4)
    c: Vertical(g5)
    c: Equal(g5,g4)
FEATURE [PartDesign::Pocket] Pocket004
  BaseFeature = -> Pocket003
  Direction = (0,1,-2e-16)
  Length = 5
  Length2 = 5
  Profile = -> Sketch019
  ReferenceAxis = -> Sketch019 [N_Axis]
  Type = 0
FEATURE [PartDesign::Body] Body017  label="Body018"
  BaseFeature = -> Cut002
  Group = -> [Clone018,Sketch016,Pocket001,Sketch017,Pocket002,Sketch018,Pocket003,Sketch019,Pocket004]
  Origin = -> Origin020
  Tip = -> Pocket004
FEATURE [Part::Cone] Cone001  label="Конус001"
  Angle = 360
  AttacherType = Attacher::AttachEngine3D
  Height = 10
  Placement = pos=(-43.64,0.39,17.17) rot=(0,0,1;0rad)
  Radius1 = 3
  Radius2 = 4
FEATURE [Part::Cone] Cone002  label="Конус002"
  Angle = 360
  AttacherType = Attacher::AttachEngine3D
  Height = 10
  Placement = pos=(-43.64,0.39,17.17) rot=(0,0,1;0rad)
  Radius1 = 3
  Radius2 = 4
FEATURE [Part::Cone] Cone003  label="Конус003"
  Angle = 360
  AttacherType = Attacher::AttachEngine3D
  Height = 10
  Placement = pos=(-43.64,0.39,17.17) rot=(0,0,1;0rad)
  Radius1 = 3
  Radius2 = 4
FEATURE [Part::Cylinder] Cylinder024  label="Цилиндр023"
  Angle = 360
  AttacherType = Attacher::AttachEngine3D
  FirstAngle = 0
  Height = 22
  Placement = pos=(-43.635,0.385,10.17) rot=(0,0,1;0rad)
  Radius = 3
  SecondAngle = 0
FEATURE [Part::Cylinder] Cylinder025  label="Цилиндр024"
  Angle = 360
  AttacherType = Attacher::AttachEngine3D
  FirstAngle = 0
  Height = 7
  Placement = pos=(-43.64,0.39,27.17) rot=(0,0,1;0rad)
  Radius = 3
  SecondAngle = 0
FEATURE [Part::Cylinder] Cylinder002  label="Цилиндр025"
  Angle = 360
  AttacherType = Attacher::AttachEngine3D
  FirstAngle = 0
  Height = 22
  Placement = pos=(-43.635,0.385,10.17) rot=(0,0,1;0rad)
  Radius = 3
  SecondAngle = 0
FEATURE [Part::Cylinder] Cylinder003  label="Цилиндр003"
  Angle = 360
  AttacherType = Attacher::AttachEngine3D
  FirstAngle = 0
  Height = 7
  Placement = pos=(-43.64,0.39,27.17) rot=(0,0,1;0rad)
  Radius = 3
  SecondAngle = 0
FEATURE [Part::Cylinder] Cylinder004  label="Цилиндр004"
  Angle = 360
  AttacherType = Attacher::AttachEngine3D
  FirstAngle = 0
  Height = 22
  Placement = pos=(-43.635,0.385,10.17) rot=(0,0,1;0rad)
  Radius = 3
  SecondAngle = 0
FEATURE [Part::Cylinder] Cylinder005  label="Цилиндр005"
  Angle = 360
  AttacherType = Attacher::AttachEngine3D
  FirstAngle = 0
  Height = 7
  Placement = pos=(-43.64,0.39,27.17) rot=(0,0,1;0rad)
  Radius = 3
  SecondAngle = 0
FEATURE [Part::Fillet] Fillet020
  Base = -> Cylinder025
  Edges = 1 edges r=1: [Edge3]
FEATURE [Part::Fillet] Fillet021
  Base = -> Cylinder024
  Edges = 1 edges r=0.5: [Edge2]
FEATURE [Part::Fillet] Fillet022
  Base = -> Cylinder003
  Edges = 1 edges r=1: [Edge3]
FEATURE [Part::Fillet] Fillet023
  Base = -> Cylinder002
  Edges = 1 edges r=0.5: [Edge2]
FEATURE [Part::Fillet] Fillet024
  Base = -> Cylinder005
  Edges = 1 edges r=1: [Edge3]
FEATURE [Part::Fillet] Fillet025
  Base = -> Cylinder004
  Edges = 1 edges r=0.5: [Edge2]
FEATURE [Part::MultiFuse] Fusion016  label="кнопка 1"
  Shapes = -> [Fillet020,Fillet021,Cone001]
FEATURE [Part::MultiFuse] Fusion017  label="кнопка 2"
  Placement = pos=(7.62,-10.16,0) rot=(0,0,1;0rad)
  Shapes = -> [Fillet022,Fillet023,Cone002]
FEATURE [Part::MultiFuse] Fusion018  label="кнопка 3"
  Placement = pos=(15.342,-20.315,0) rot=(0,0,1;0rad)
  Shapes = -> [Fillet024,Fillet025,Cone003]
FEATURE [Part::Compound] Compound001  label="кнопки"
  Links = -> [Fusion016,Fusion017,Fusion018]
  Placement = pos=(0,0,9) rot=(0,0,1;0rad)
FEATURE [Sketcher::SketchObject] Sketch020
  FullyConstrained = false
  MapMode = 5
  Placement = pos=(0,0,40.58) rot=(0,0,1;0rad)
  Support = -> [Clone017]
  sketch-geometry (3):
    g0: Circle CenterX=-43.64 CenterY=0.39 CenterZ=0 NormalX=0 NormalY=0 NormalZ=1 AngleXU=0 Radius=3.25
    g1: Circle CenterX=-36.02 CenterY=-9.77 CenterZ=0 NormalX=0 NormalY=0 NormalZ=1 AngleXU=0 Radius=3.25
    g2: Circle CenterX=-28.298 CenterY=-19.925 CenterZ=0 NormalX=0 NormalY=0 NormalZ=1 AngleXU=0 Radius=3.25
  constraints (3):
    c: Diameter(g2) = 6.5
    c: Diameter(g0) = 6.5
    c: Diameter(g1) = 6.5
FEATURE [PartDesign::Hole] Hole
  BaseFeature = -> Clone017
  CustomThreadClearance = 0
  Depth = 25
  DepthType = 0
  Diameter = 6.2
  DrillForDepth = false
  DrillPoint = 1
  DrillPointAngle = 118
  HoleCutCountersinkAngle = 90
  HoleCutCustomValues = false
  HoleCutDepth = 0
  HoleCutDiameter = 6.1
  HoleCutType = 0
  ModelThread = false
  Profile = -> Sketch020
  Tapered = false
  TaperedAngle = 90
  ThreadClass = 0
  ThreadDepth = 25
  ThreadDepthType = 0
  ThreadDirection = 0
  ThreadFit = 0
  ThreadSize = 0
  ThreadType = 0
  Threaded = false
  UseCustomThreadClearance = false
FEATURE [Sketcher::SketchObject] Sketch021
  ExternalGeometry = -> [Hole]
  FullyConstrained = true
  MapMode = 5
  Placement = pos=(0,0,40.58) rot=(0,0,1;0rad)
  Support = -> [Hole]
  sketch-geometry (6):
    g0: Circle CenterX=-43.64 CenterY=0.39 CenterZ=0 NormalX=0 NormalY=0 NormalZ=1 AngleXU=0 Radius=4.1
    g1: Circle CenterX=-43.64 CenterY=0.39 CenterZ=0 NormalX=0 NormalY=0 NormalZ=1 AngleXU=0 Radius=4.6
    g2: Circle CenterX=-36.02 CenterY=-9.77 CenterZ=0 NormalX=0 NormalY=0 NormalZ=1 AngleXU=0 Radius=4.1
    g3: Circle CenterX=-36.02 CenterY=-9.77 CenterZ=0 NormalX=0 NormalY=0 NormalZ=1 AngleXU=0 Radius=4.6
    g4: Circle CenterX=-28.298 CenterY=-19.925 CenterZ=0 NormalX=0 NormalY=0 NormalZ=1 AngleXU=0 Radius=4.1
    g5: Circle CenterX=-28.298 CenterY=-19.925 CenterZ=0 NormalX=0 NormalY=0 NormalZ=1 AngleXU=0 Radius=4.6
  constraints (12):
    c: Coincident(g0,g-3)
    c: Diameter(g0) = 8.2
    c: Coincident(g1,g0)
    c: Diameter(g1) = 9.2
    c: Coincident(g2,g-4)
    c: Coincident(g3,g2)
    c: Diameter(g2) = 8.2
    c: Diameter(g3) = 9.2
    c: Coincident(g4,g-5)
    c: Coincident(g5,g4)
    c: Diameter(g4) = 8.2
    c: Diameter(g5) = 9.2
FEATURE [Part::Part2DObjectPython] ShapeString  # Draft 2D object (typed FeaturePython)
  FontFile = <path>
  MakeFace = true
  Placement = pos=(45.4276,0.416211,6.58) rot=(0,1,0;3.14159rad)
  Size = 10
  String = IOTV_ID4.1
  Tracking = 0
FEATURE [Part::Extrusion] Extrude004
  Base = -> ShapeString
  Dir = (0,8.74228e-08,-1)
  DirMode = 2
  FaceMakerClass = Part::FaceMakerBullseye
  LengthFwd = 10
  LengthRev = 0
  Placement = pos=(0,0,1) rot=(0,0,1;0rad)
  Solid = false
  Symmetric = false
FEATURE [PartDesign::Pad] Pad001
  BaseFeature = -> Hole
  Direction = (0,0,1)
  Length = 22
  Length2 = 10
  Profile = -> Sketch021
  ReferenceAxis = -> Sketch021 [N_Axis]
  Reversed = true
  Type = 0
FEATURE [PartDesign::Fillet] Fillet026
  Base = -> Pad001 [Edge173,Edge193,Edge202,Edge185]
  BaseFeature = -> Pad001
  Radius = 4
  SupportTransform = false
  UseAllEdges = false
FEATURE [PartDesign::Body] Body016  label="Body017"
  BaseFeature = -> Cut004
  Group = -> [Clone017,Sketch020,Hole,Sketch021,Pad001,Fillet026]
  Origin = -> Origin018
  Tip = -> Fillet026
FEATURE [App::Part] Part001  label="крышка003"
  Group = -> [Body011,Body015,Cylinder023,Array,Array001,Clone016,Body016]
  Origin = -> Origin012
FEATURE [Part::Cut] Cut005
  Base = -> Body017
  Tool = -> Extrude004
FEATURE [PartDesign::FeatureBase] Clone019
  BaseFeature = -> Cut005
FEATURE [PartDesign::Body] Body018  label="Body019"
  BaseFeature = -> Cut005
  Group = -> [Clone019]
  Origin = -> Origin022
  Tip = -> Clone019
FEATURE [App::Part] Part  label="корпус002"
  Group = -> [Body,ShapeBinder,ShapeBinder001,ShapeBinder002,ShapeBinder003,Loft,Body003,Body004,Body005,Cylinder001,Clone009,Cut001,Fusion004,Cut,Cut002,Body017,ShapeString,Body018]
  Origin = -> Origin011
FEATURE [PartDesign::FeatureBase] Clone020
  BaseFeature = -> Compound001
  Placement = pos=(0,0,9) rot=(0,0,1;0rad)
FEATURE [Sketcher::SketchObject] Sketch022
  ExternalGeometry = -> [Clone020]
  FullyConstrained = false
  MapMode = 5
  Placement = pos=(0,0,43.17) rot=(0,0,1;0rad)
  Support = -> [Clone020]
  sketch-geometry (46):
    g0: LineSegment StartX=-43.529 StartY=1.14 StartZ=0 EndX=-42.029 EndY=1.14 EndZ=0
    g1: LineSegment StartX=-42.029 StartY=1.14 StartZ=0 EndX=-42.029 EndY=-0.36 EndZ=0
    g2: LineSegment StartX=-42.029 StartY=-0.36 StartZ=0 EndX=-43.529 EndY=-0.36 EndZ=0
    g3: LineSegment StartX=-43.529 StartY=-0.36 StartZ=0 EndX=-43.529 EndY=1.14 EndZ=0
    g4: LineSegment StartX=-45.3026 StartY=1.14 StartZ=0 EndX=-45.3026 EndY=-0.36 EndZ=0
    g5: LineSegment StartX=-45.3026 StartY=-0.36 StartZ=0 EndX=-44.0035 EndY=0.39 EndZ=0
    g6: LineSegment StartX=-44.0035 StartY=0.39 StartZ=0 EndX=-45.3026 EndY=1.14 EndZ=0
    g7: LineSegment StartX=-43.9152 StartY=1.39 StartZ=0 EndX=-43.9152 EndY=-0.61 EndZ=0
    g8: LineSegment StartX=-43.9152 StartY=-0.61 StartZ=0 EndX=-43.7152 EndY=-0.61 EndZ=0
    g9: LineSegment StartX=-43.7152 StartY=-0.61 StartZ=0 EndX=-43.7152 EndY=1.39 EndZ=0
    g10: LineSegment StartX=-43.7152 StartY=1.39 StartZ=0 EndX=-43.9152 EndY=1.39 EndZ=0
    g11: LineSegment StartX=-35.9346 StartY=-8.48383 StartZ=0 EndX=-35.0089 EndY=-8.48383 EndZ=0
    g12: LineSegment StartX=-35.0089 StartY=-8.48383 StartZ=0 EndX=-35.0089 EndY=-8.78206 EndZ=0
    g13: LineSegment StartX=-35.0089 StartY=-8.78206 StartZ=0 EndX=-35.7065 EndY=-8.78206 EndZ=0
    g14: LineSegment StartX=-35.7065 StartY=-8.78206 StartZ=0 EndX=-35.7065 EndY=-10.4804 EndZ=0
    g15: ArcOfCircle CenterX=-36.2465 CenterY=-10.4804 CenterZ=0 NormalX=0 NormalY=0 NormalZ=1 AngleXU=0 Radius=0.540033 StartAngle=0.955025 EndAngle=6.28319
    g16: LineSegment StartX=-35.9346 StartY=-8.48383 StartZ=0 EndX=-35.9346 EndY=-10.0396 EndZ=0
    g17: LineSegment StartX=-28.7347 StartY=-20.7106 StartZ=0 EndX=-28.7347 EndY=-21.3717 EndZ=0
    g18: LineSegment StartX=-28.4881 StartY=-21.6183 StartZ=0 EndX=-28.1089 EndY=-21.6183 EndZ=0
    g19: LineSegment StartX=-27.8623 StartY=-21.3717 StartZ=0 EndX=-27.8623 EndY=-20.7106 EndZ=0
    g20: ArcOfCircle CenterX=-28.3048 CenterY=-19.684 CenterZ=0 NormalX=0 NormalY=0 NormalZ=1 AngleXU=0 Radius=0.905334 StartAngle=5.43599 EndAngle=10.2922
    g21: ArcOfCircle CenterX=-28.4881 CenterY=-21.3717 CenterZ=0 NormalX=0 NormalY=0 NormalZ=1 AngleXU=0 Radius=0.24657 StartAngle=3.14159 EndAngle=4.71239
    g22: ArcOfCircle CenterX=-28.1089 CenterY=-21.3717 CenterZ=0 NormalX=0 NormalY=0 NormalZ=1 AngleXU=0 Radius=0.24657 StartAngle=4.71239 EndAngle=6.28319
    g23: ArcOfCircle CenterX=-29.1754 CenterY=-20.7106 CenterZ=0 NormalX=0 NormalY=0 NormalZ=1 AngleXU=0 Radius=0.440712 StartAngle=2e-16 EndAngle=0.86741
    g24: ArcOfCircle CenterX=-27.3978 CenterY=-20.7106 CenterZ=0 NormalX=0 NormalY=0 NormalZ=1 AngleXU=0 Radius=0.464468 StartAngle=2.29439 EndAngle=3.14159
    g25: LineSegment StartX=-28.4104 StartY=-18.0606 StartZ=0 EndX=-28.2104 EndY=-18.0606 EndZ=0
    g26: LineSegment StartX=-28.2104 StartY=-18.0606 StartZ=0 EndX=-28.2104 EndY=-18.6606 EndZ=0
    g27: LineSegment StartX=-28.2104 StartY=-18.6606 StartZ=0 EndX=-28.4104 EndY=-18.6606 EndZ=0
    g28: LineSegment StartX=-28.4104 StartY=-18.6606 StartZ=0 EndX=-28.4104 EndY=-18.0606 EndZ=0
    g29: LineSegment StartX=-30.0349 StartY=-19.7244 StartZ=0 EndX=-29.4349 EndY=-19.7244 EndZ=0
    g30: LineSegment StartX=-29.4349 StartY=-19.7244 StartZ=0 EndX=-29.4349 EndY=-19.9244 EndZ=0
    g31: LineSegment StartX=-29.4349 StartY=-19.9244 StartZ=0 EndX=-30.0349 EndY=-19.9244 EndZ=0
    g32: LineSegment StartX=-30.0349 StartY=-19.9244 StartZ=0 EndX=-30.0349 EndY=-19.7244 EndZ=0
    g33: LineSegment StartX=-27.1317 StartY=-19.7244 StartZ=0 EndX=-26.5317 EndY=-19.7244 EndZ=0
    g34: LineSegment StartX=-26.5317 StartY=-19.7244 StartZ=0 EndX=-26.5317 EndY=-19.9244 EndZ=0
    g35: LineSegment StartX=-26.5317 StartY=-19.9244 StartZ=0 EndX=-27.1317 EndY=-19.9244 EndZ=0
    g36: LineSegment StartX=-27.1317 StartY=-19.9244 StartZ=0 EndX=-27.1317 EndY=-19.7244 EndZ=0
    g37: LineSegment StartX=-27.3296 StartY=-19.0575 StartZ=0 EndX=-26.9054 EndY=-18.6333 EndZ=0
    g38: LineSegment StartX=-27.1882 StartY=-19.199 StartZ=0 EndX=-26.7639 EndY=-18.7747 EndZ=0
    g39: LineSegment StartX=-26.9054 StartY=-18.6333 StartZ=0 EndX=-26.7639 EndY=-18.7747 EndZ=0
    g40: LineSegment StartX=-27.1882 StartY=-19.199 StartZ=0 EndX=-27.3296 EndY=-19.0575 EndZ=0
    g41: LineSegment StartX=-29.3598 StartY=-19.199 StartZ=0 EndX=-29.2184 EndY=-19.0575 EndZ=0
    g42: LineSegment StartX=-29.2184 StartY=-19.0575 StartZ=0 EndX=-29.6325 EndY=-18.6234 EndZ=0
    g43: LineSegment StartX=-29.6325 StartY=-18.6234 StartZ=0 EndX=-29.774 EndY=-18.7648 EndZ=0
    g44: LineSegment StartX=-29.774 StartY=-18.7648 StartZ=0 EndX=-29.3598 EndY=-19.199 EndZ=0
    g45: LineSegment StartX=-29.7316 StartY=-19.199 StartZ=0 EndX=-29.3598 EndY=-19.199 EndZ=0
  constraints (106):
    c: Coincident(g0,g1)
    c: Coincident(g1,g2)
    c: Coincident(g2,g3)
    c: Coincident(g3,g0)
    c: Horizontal(g0)
    c: Horizontal(g2)
    c: Vertical(g1)
    c: Vertical(g3)
    c: Vertical(g4)
    c: Coincident(g5,g4)
    c: Coincident(g6,g5)
    c: Coincident(g6,g4)
    c: Vertical(g7)
    c: Coincident(g9,g8)
    c: Vertical(g9)
    c: Coincident(g10,g9)
    c: Coincident(g10,g7)
    c: Coincident(g7,g8)
    c: Horizontal(g8)
    c: Horizontal(g10)
    c: Angle(g5,g4) = 1.0472
    c: Angle(g4,g6) = 1.0472
    c: Equal(g0,g1)
    c: Distance(g1) = 1.5
    c: Distance(g4) = 1.5
    c: Distance(g7) = 2
    c: DistanceY(g-3,g5) = 0
    c: DistanceY(g4,g2) = 0
    c: DistanceY(g0,g9) = 0.25
    c: Distance(g8) = 0.2
    c: Coincident(g12,g11)
    c: Vertical(g12)
    c: Horizontal(g13)
    c: Horizontal(g11)
    c: Coincident(g13,g12)
    c: Coincident(g14,g13)
    c: Vertical(g14)
    c: Coincident(g16,g11)
    c: Vertical(g16)
    c: Tangent(g15,g14) = 1.5708
    c: Coincident(g15,g16)
    c: Vertical(g17)
    c: Horizontal(g18)
    c: Vertical(g19)
    c: Equal(g17,g19)
    c: Tangent(g17,g21) = -1.5708
    c: Tangent(g18,g21) = -1.5708
    c: Tangent(g19,g22) = -1.5708
    c: Tangent(g18,g22) = -1.5708
    c: Equal(g21,g22)
    c: Tangent(g20,g23) = 1.5708
    c: Tangent(g17,g23) = 1.5708
    c: Tangent(g20,g24) = 1.5708
    c: Tangent(g19,g24) = 1.5708
    c: Coincident(g25,g26)
    c: Coincident(g26,g27)
    c: Coincident(g27,g28)
    c: Coincident(g28,g25)
    c: Horizontal(g25)
    c: Horizontal(g27)
    c: Vertical(g26)
    c: Vertical(g28)
    c: Coincident(g29,g30)
    c: Coincident(g30,g31)
    c: Coincident(g31,g32)
    c: Coincident(g32,g29)
    c: Horizontal(g29)
    c: Horizontal(g31)
    c: Vertical(g30)
    c: Vertical(g32)
    c: Coincident(g33,g34)
    c: Coincident(g34,g35)
    c: Coincident(g35,g36)
    c: Coincident(g36,g33)
    c: Horizontal(g33)
    c: Horizontal(g35)
    c: Vertical(g34)
    c: Vertical(g36)
    c: Coincident(g39,g37)
    c: Coincident(g39,g38)
    c: Coincident(g40,g38)
    c: Coincident(g40,g37)
    c: Coincident(g42,g41)
    c: Coincident(g44,g43)
    c: Coincident(g44,g41)
    c: Equal(g33,g29)
    c: Equal(g32,g36)
    c: DistanceY(g29,g33) = 0
    c: Distance(g32) = 0.2
    c: Equal(g29,g28)
    c: Equal(g27,g30)
    c: Parallel(g44,g42)
    c: Parallel(g41,g43)
    c: Coincident(g43,g42)
    c: Horizontal(g45)
    c: Coincident(g45,g41)
    c: Distance(g41) = 0.2
    c: Angle(g41,g45) = 2.35619
    c: Distance(g28) = 0.6
    c: DistanceY(g41,g37) = 0
    c: DistanceY(g41,g38) = 0
    c: Angle(g38,g45) = 2.35619
    c: Equal(g40,g39)
    c: Parallel(g39,g40)
    c: Angle(g40,g45) = 0.785398
    c: Equal(g37,g42)
FEATURE [PartDesign::Body] Body019  label="Body020"
  BaseFeature = -> Compound001
  Group = -> [Clone020,Sketch022]
  Origin = -> Origin023
  Tip = -> Clone020
FEATURE [Part::Extrusion] Extrude005
  Base = -> Sketch022
  Dir = (0,0,1)
  DirMode = 2
  FaceMakerClass = Part::FaceMakerBullseye
  LengthFwd = 1
  LengthRev = 0
  Solid = true
  Symmetric = false
FEATURE [Part::MultiFuse] Fusion019
  Shapes = -> [Extrude005,Body019]
FEATURE [PartDesign::FeatureBase] Clone021
  BaseFeature = -> Fusion019
FEATURE [PartDesign::Body] Body020  label="Body021"
  BaseFeature = -> Fusion019
  Group = -> [Clone021]
  Origin = -> Origin024
  Tip = -> Clone021
FEATURE [App::Part] Part003  label="кнопки001"
  Group = -> [Cylinder024,Fillet021,Fillet022,Fillet023,Fillet024,Fillet025,Fusion016,Fusion017,Fusion018,Cylinder025,Cylinder002,Cylinder003,Cylinder004,Cylinder005,Cone001,Cone002,Cone003,Fillet020,Compound001,Body019,Body020]
  Origin = -> Origin021
note: 1 file-system path scrubbed to <path> (originals preserved in the JSON sidecar)
